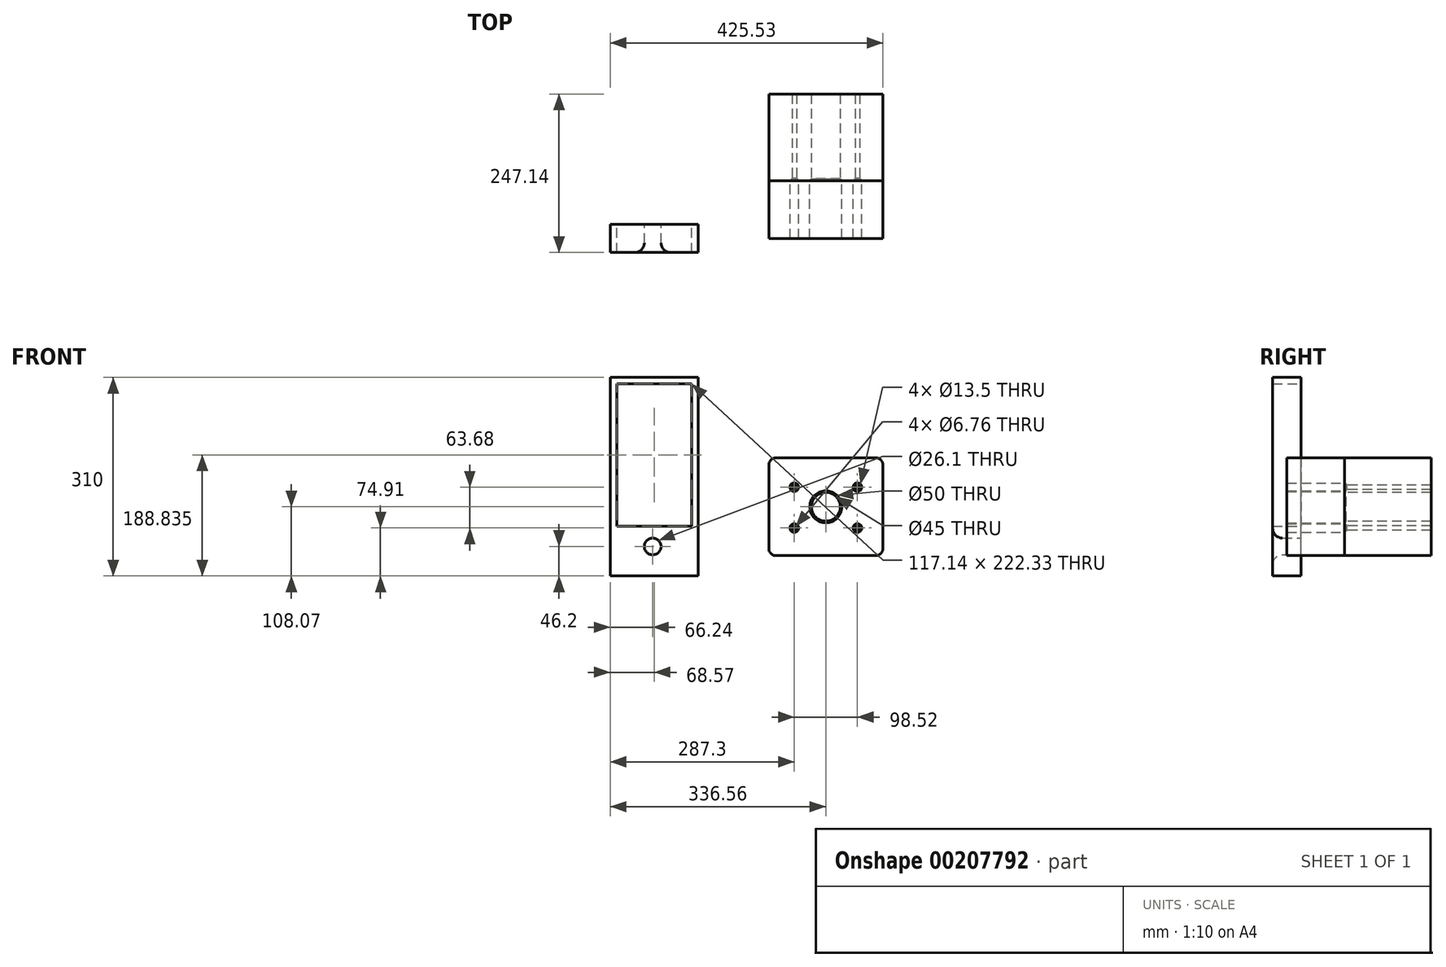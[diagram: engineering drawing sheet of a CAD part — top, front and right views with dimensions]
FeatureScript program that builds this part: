
annotation { "Feature Type Name" : "Feature", "Feature Type Description" : "" }
export const myFeature = defineFeature(function(context is Context, id is Id, definition is map)
    precondition{}
    {
        {
            var Q0;
            Q0=qCreatedBy(makeId("Front.planeOp"),FACE);
            var sketch = newSketch(context, id + "F0", { "sketchPlane" : qUnion([Q0])});
            skLineSegment(sketch, "E0.bottom", {"start": v(-88.97, 76.32) * mm, "end": v(88.97, 76.32) * mm});
            skLineSegment(sketch, "E0.top", {"start": v(-88.97, -76.32) * mm, "end": v(88.97, -76.32) * mm});
            skLineSegment(sketch, "E0.left", {"start": v(-88.97, 76.32) * mm, "end": v(-88.97, -76.32) * mm});
            skLineSegment(sketch, "E0.right", {"start": v(88.97, 76.32) * mm, "end": v(88.97, -76.32) * mm});
            skPoint(sketch, "E0.middle", {"position": v(0, 0) * mm});
            skSolve(sketch);
        }
        {
            var Q0;
            Q0 = qSketchRegion(id + "F0", true);
            extrude(context, id + "F1", {"entities" : qUnion([Q0]), "endBound" : BoundingType.SYMMETRIC, "depth" : 135.13 * mm});
        }
        {
            var Q0;
            Q0=makeQuery(id+"F1.opExtrude","SWEPT_EDGE",EDGE,{"disambiguationData":[OSD([sQuery(id+"F0.wireOp",EDGE,"E0.bottom"),sQuery(id+"F0.wireOp",EDGE,"E0.right")])]});
            var Q1;
            Q1=makeQuery(id+"F1.opExtrude","SWEPT_EDGE",EDGE,{"disambiguationData":[OSD([sQuery(id+"F0.wireOp",EDGE,"E0.top"),sQuery(id+"F0.wireOp",EDGE,"E0.right")])]});
            var Q2;
            Q2=makeQuery(id+"F1.opExtrude","SWEPT_EDGE",EDGE,{"disambiguationData":[OSD([sQuery(id+"F0.wireOp",EDGE,"E0.top"),sQuery(id+"F0.wireOp",EDGE,"E0.left")])]});
            var Q3;
            Q3=makeQuery(id+"F1.opExtrude","SWEPT_EDGE",EDGE,{"disambiguationData":[OSD([sQuery(id+"F0.wireOp",EDGE,"E0.bottom"),sQuery(id+"F0.wireOp",EDGE,"E0.left")])]});
            fillet(context, id + "F2", {"entities" : qUnion([Q0, Q1, Q2, Q3]), "radius" : 11 * mm, "tangentPropagation" : true, "allowEdgeOverflow" : false});
        }
        {
            var Q0;
            Q0=makeQuery(id+"F1.opExtrude","CAP_FACE",FACE,{"disambiguationData":[OSD([sQuery(id+"F0.wireOp",EDGE,"E0.bottom"),sQuery(id+"F0.wireOp",EDGE,"E0.top"),sQuery(id+"F0.wireOp",EDGE,"E0.left"),sQuery(id+"F0.wireOp",EDGE,"E0.right")])],"isStart":false});
            var sketch = newSketch(context, id + "F3", { "sketchPlane" : qUnion([Q0])});
            skLineSegment(sketch, "E1.bottom", {"start": v(-49.26, 30.52) * mm, "end": v(49.26, 30.52) * mm});
            skLineSegment(sketch, "E1.top", {"start": v(-49.26, -33.16) * mm, "end": v(49.26, -33.16) * mm});
            skLineSegment(sketch, "E1.left", {"start": v(-49.26, 30.52) * mm, "end": v(-49.26, -33.16) * mm});
            skLineSegment(sketch, "E1.right", {"start": v(49.26, 30.52) * mm, "end": v(49.26, -33.16) * mm});
            skPoint(sketch, "E1.middle", {"position": v(0, -1.32) * mm});
            skSolve(sketch);
        }
        {
            var Q0;
            Q0=sQuery(id+"F3.wireOp",VERTEX,"E1.bottom.start");
            var Q1;
            Q1=sQuery(id+"F3.wireOp",VERTEX,"E1.right.start");
            var Q2;
            Q2=sQuery(id+"F3.wireOp",VERTEX,"E1.right.end");
            var Q3;
            Q3=sQuery(id+"F3.wireOp",VERTEX,"E1.left.end");
            var Q4;
            Q4=makeQuery(id+"F1.opExtrude","SWEPT_BODY",BODY,{"disambiguationData":[OSD([sQuery(id+"F0.wireOp",EDGE,"E0.bottom"),sQuery(id+"F0.wireOp",EDGE,"E0.top"),sQuery(id+"F0.wireOp",EDGE,"E0.left"),sQuery(id+"F0.wireOp",EDGE,"E0.right")])]});
            hole(context, id + "F4", {"style" : HoleStyle.C_SINK, "endStyle" : HoleEndStyle.THROUGH, "holeDiameter" : 6.76 * mm, "cSinkDiameter" : 13.5 * mm, "cSinkAngle" : 82 * degree, "locations" : qUnion([Q0, Q1, Q2, Q3]), "scope" : qUnion([Q4]), "isTappedThrough" : true});
        }
        {
            var Q0;
            Q0=makeQuery(id+"F1.opExtrude","CAP_FACE",FACE,{"disambiguationData":[OSD([sQuery(id+"F0.wireOp",EDGE,"E0.bottom"),sQuery(id+"F0.wireOp",EDGE,"E0.top"),sQuery(id+"F0.wireOp",EDGE,"E0.left"),sQuery(id+"F0.wireOp",EDGE,"E0.right")])],"isStart":false});
            var sketch = newSketch(context, id + "F5", { "sketchPlane" : qUnion([Q0])});
            skLineSegment(sketch, "E2.bottom", {"start": v(-27.1, -25.07) * mm, "end": v(27.1, -25.07) * mm});
            skLineSegment(sketch, "E2.top", {"start": v(-27.1, 25.07) * mm, "end": v(27.1, 25.07) * mm});
            skLineSegment(sketch, "E2.left", {"start": v(-27.1, -25.07) * mm, "end": v(-27.1, 25.07) * mm});
            skLineSegment(sketch, "E2.right", {"start": v(27.1, -25.07) * mm, "end": v(27.1, 25.07) * mm});
            skPoint(sketch, "E2.middle", {"position": v(0, 0) * mm});
            skSolve(sketch);
        }
        {
            var Q0;
            Q0=sQuery(id+"F5.wireOp",VERTEX,"E2.middle");
            var Q1;
            Q1=makeQuery(id+"F1.opExtrude","SWEPT_BODY",BODY,{"disambiguationData":[OSD([sQuery(id+"F0.wireOp",EDGE,"E0.bottom"),sQuery(id+"F0.wireOp",EDGE,"E0.top"),sQuery(id+"F0.wireOp",EDGE,"E0.left"),sQuery(id+"F0.wireOp",EDGE,"E0.right")])]});
            hole(context, id + "F6", {"style" : HoleStyle.C_SINK, "endStyle" : HoleEndStyle.THROUGH, "holeDiameter" : 45 * mm, "cSinkDiameter" : 50 * mm, "cSinkAngle" : 82 * degree, "locations" : qUnion([Q0]), "scope" : qUnion([Q1]), "isTappedThrough" : true});
        }
        {
            var Q0;
            Q0=makeQuery(id+"F1.opExtrude","CAP_FACE",FACE,{"disambiguationData":[OSD([sQuery(id+"F0.wireOp",EDGE,"E0.bottom"),sQuery(id+"F0.wireOp",EDGE,"E0.top"),sQuery(id+"F0.wireOp",EDGE,"E0.left"),sQuery(id+"F0.wireOp",EDGE,"E0.right")])],"isStart":false});
            extrude(context, id + "F7", {"entities" : qUnion([Q0]), "depth" : 90 * mm});
        }
        {
            var Q0;
            Q0=makeQuery(id+"F7.opExtrude","CAP_FACE",FACE,{"disambiguationData":[OSD([sQuery(id+"F0.wireOp",EDGE,"E0.bottom"),sQuery(id+"F0.wireOp",EDGE,"E0.top"),sQuery(id+"F0.wireOp",EDGE,"E0.left"),sQuery(id+"F0.wireOp",EDGE,"E0.right")])],"isStart":false});
            var sketch = newSketch(context, id + "F8", { "sketchPlane" : qUnion([Q0])});
            skLineSegment(sketch, "E3.bottom", {"start": v(-199.42, -108.07) * mm, "end": v(-336.56, -108.07) * mm});
            skLineSegment(sketch, "E3.top", {"start": v(-199.42, 201.93) * mm, "end": v(-336.56, 201.93) * mm});
            skLineSegment(sketch, "E3.left", {"start": v(-199.42, -108.07) * mm, "end": v(-199.42, 201.93) * mm});
            skLineSegment(sketch, "E3.right", {"start": v(-336.56, -108.07) * mm, "end": v(-336.56, 201.93) * mm});
            skPoint(sketch, "E3.middle", {"position": v(-268, 46.93) * mm});
            skLineSegment(sketch, "E4.bottom", {"start": v(-326.56, 191.93) * mm, "end": v(-209.42, 191.93) * mm});
            skLineSegment(sketch, "E4.top", {"start": v(-326.56, -98.07) * mm, "end": v(-209.42, -98.07) * mm});
            skLineSegment(sketch, "E4.left", {"start": v(-326.56, 191.93) * mm, "end": v(-326.56, -98.07) * mm});
            skLineSegment(sketch, "E4.right", {"start": v(-209.42, 191.93) * mm, "end": v(-209.42, -98.07) * mm});
            skLineSegment(sketch, "E5.top", {"start": v(-326.56, -30.4) * mm, "end": v(-209.42, -30.4) * mm});
            skLineSegment(sketch, "E5.left", {"start": v(-326.56, -98.07) * mm, "end": v(-326.56, -30.4) * mm});
            skLineSegment(sketch, "E5.right", {"start": v(-209.42, -98.07) * mm, "end": v(-209.42, -30.4) * mm});
            skCircle(sketch, "E6", {"center": v(-270.32, -61.87) * mm, "radius": 13.05 * mm});
            skSolve(sketch);
        }
        {
            var Q0;
            Q0=makeQuery(id+"F8.imprint","IMPRINT",FACE,{"disambiguationData":[TD([[makeQuery(id+"F8.imprint","IMPRINT",EDGE,{"derivedFrom":sQuery(id+"F8.wireOp",EDGE,"E3.bottom")}),-1.0]])]});
            var Q1;
            Q1=makeQuery(id+"F8.imprint","IMPRINT",FACE,{"disambiguationData":[TD([[makeQuery(id+"F8.imprint","IMPRINT",EDGE,{"derivedFrom":sQuery(id+"F8.wireOp",EDGE,"E4.top")}),1.0]])]});
            extrude(context, id + "F9", {"entities" : qUnion([Q0, Q1]), "endBound" : BoundingType.SYMMETRIC, "depth" : 44 * mm});
        }
        {
            var Q0;
            Q0=makeQuery(id+"F9.opExtrude","CAP_EDGE",EDGE,{"disambiguationData":[OSD([sQuery(id+"F8.wireOp",EDGE,"E6")])],"isStart":false});
            fillet(context, id + "F10", {"entities" : qUnion([Q0]), "radius" : 15 * mm, "tangentPropagation" : true, "allowEdgeOverflow" : false});
        }
    });
